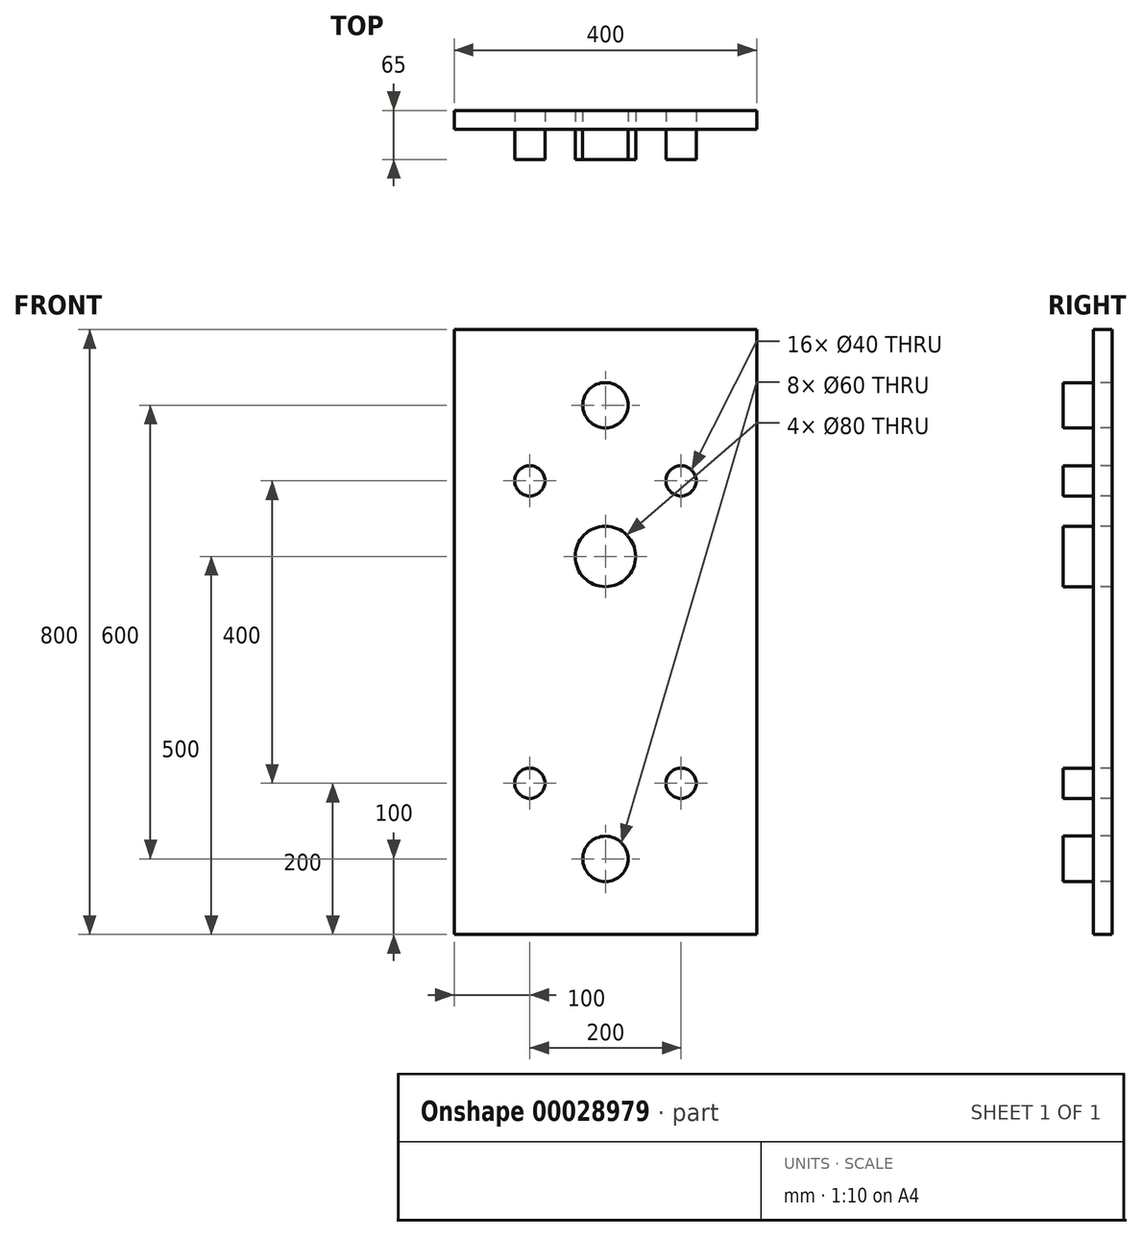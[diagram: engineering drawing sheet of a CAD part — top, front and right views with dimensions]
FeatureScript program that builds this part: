
annotation { "Feature Type Name" : "Feature", "Feature Type Description" : "" }
export const myFeature = defineFeature(function(context is Context, id is Id, definition is map)
    precondition{}
    {
        {
            var Q0;
            Q0=qCreatedBy(makeId("Front.planeOp"),FACE);
            var sketch = newSketch(context, id + "F0", { "sketchPlane" : qUnion([Q0])});
            skCircle(sketch, "E0", {"center": v(0, 0) * mm, "radius": 30 * mm});
            skCircle(sketch, "E1", {"center": v(-100, -100) * mm, "radius": 20 * mm});
            skCircle(sketch, "E2.0.1.0", {"center": v(-100, -500) * mm, "radius": 20 * mm});
            skCircle(sketch, "E2.1.0.0", {"center": v(100, -100) * mm, "radius": 20 * mm});
            skCircle(sketch, "E2.1.1.0", {"center": v(100, -500) * mm, "radius": 20 * mm});
            skLineSegment(sketch, "E2.direction1", {"start": v(-100, -100) * mm, "end": v(100, -100) * mm, "construction": true});
            skLineSegment(sketch, "E2.direction2", {"start": v(-100, -100) * mm, "end": v(-100, -500) * mm, "construction": true});
            skCircle(sketch, "E3", {"center": v(0, -600) * mm, "radius": 30 * mm});
            skLineSegment(sketch, "E4.bottom", {"start": v(-200, 100) * mm, "end": v(200, 100) * mm});
            skLineSegment(sketch, "E4.top", {"start": v(-200, -700) * mm, "end": v(200, -700) * mm});
            skLineSegment(sketch, "E4.left", {"start": v(-200, 100) * mm, "end": v(-200, -700) * mm});
            skLineSegment(sketch, "E4.right", {"start": v(200, 100) * mm, "end": v(200, -700) * mm});
            skCircle(sketch, "E5", {"center": v(0, -200) * mm, "radius": 40 * mm});
            skSolve(sketch);
        }
        {
            var Q0;
            Q0=makeQuery(id+"F0.imprint","IMPRINT",FACE,{"disambiguationData":[TD([[makeQuery(id+"F0.imprint","IMPRINT",EDGE,{"derivedFrom":sQuery(id+"F0.wireOp",EDGE,"E5")}),1.0]])]});
            var Q1;
            Q1=makeQuery(id+"F0.imprint","IMPRINT",FACE,{"disambiguationData":[TD([[makeQuery(id+"F0.imprint","IMPRINT",EDGE,{"derivedFrom":sQuery(id+"F0.wireOp",EDGE,"E2.1.0.0")}),1.0]])]});
            var Q2;
            Q2=makeQuery(id+"F0.imprint","IMPRINT",FACE,{"disambiguationData":[TD([[makeQuery(id+"F0.imprint","IMPRINT",EDGE,{"derivedFrom":sQuery(id+"F0.wireOp",EDGE,"E0")}),1.0]])]});
            var Q3;
            Q3=makeQuery(id+"F0.imprint","IMPRINT",FACE,{"disambiguationData":[TD([[makeQuery(id+"F0.imprint","IMPRINT",EDGE,{"derivedFrom":sQuery(id+"F0.wireOp",EDGE,"E1")}),1.0]])]});
            var Q4;
            Q4=makeQuery(id+"F0.imprint","IMPRINT",FACE,{"disambiguationData":[TD([[makeQuery(id+"F0.imprint","IMPRINT",EDGE,{"derivedFrom":sQuery(id+"F0.wireOp",EDGE,"E2.0.1.0")}),1.0]])]});
            var Q5;
            Q5=makeQuery(id+"F0.imprint","IMPRINT",FACE,{"disambiguationData":[TD([[makeQuery(id+"F0.imprint","IMPRINT",EDGE,{"derivedFrom":sQuery(id+"F0.wireOp",EDGE,"E2.1.1.0")}),1.0]])]});
            var Q6;
            Q6=makeQuery(id+"F0.imprint","IMPRINT",FACE,{"disambiguationData":[TD([[makeQuery(id+"F0.imprint","IMPRINT",EDGE,{"derivedFrom":sQuery(id+"F0.wireOp",EDGE,"E3")}),1.0]])]});
            var Q7;
            Q7=sQuery(id+"F0.wireOp",EDGE,"E4.bottom");
            extrude(context, id + "F1", {"entities" : qUnion([Q0, Q1, Q2, Q3, Q4, Q5, Q6]), "surfaceEntities" : qUnion([Q7]), "depth" : 40 * mm});
        }
        {
            var Q0;
            Q0=makeQuery(id+"F0.imprint","IMPRINT",FACE,{"disambiguationData":[TD([[makeQuery(id+"F0.imprint","IMPRINT",EDGE,{"derivedFrom":sQuery(id+"F0.wireOp",EDGE,"E0")}),-1.0]])]});
            extrude(context, id + "F2", {"entities" : qUnion([Q0]), "oppositeDirection" : true, "depth" : 25 * mm});
        }
    });
